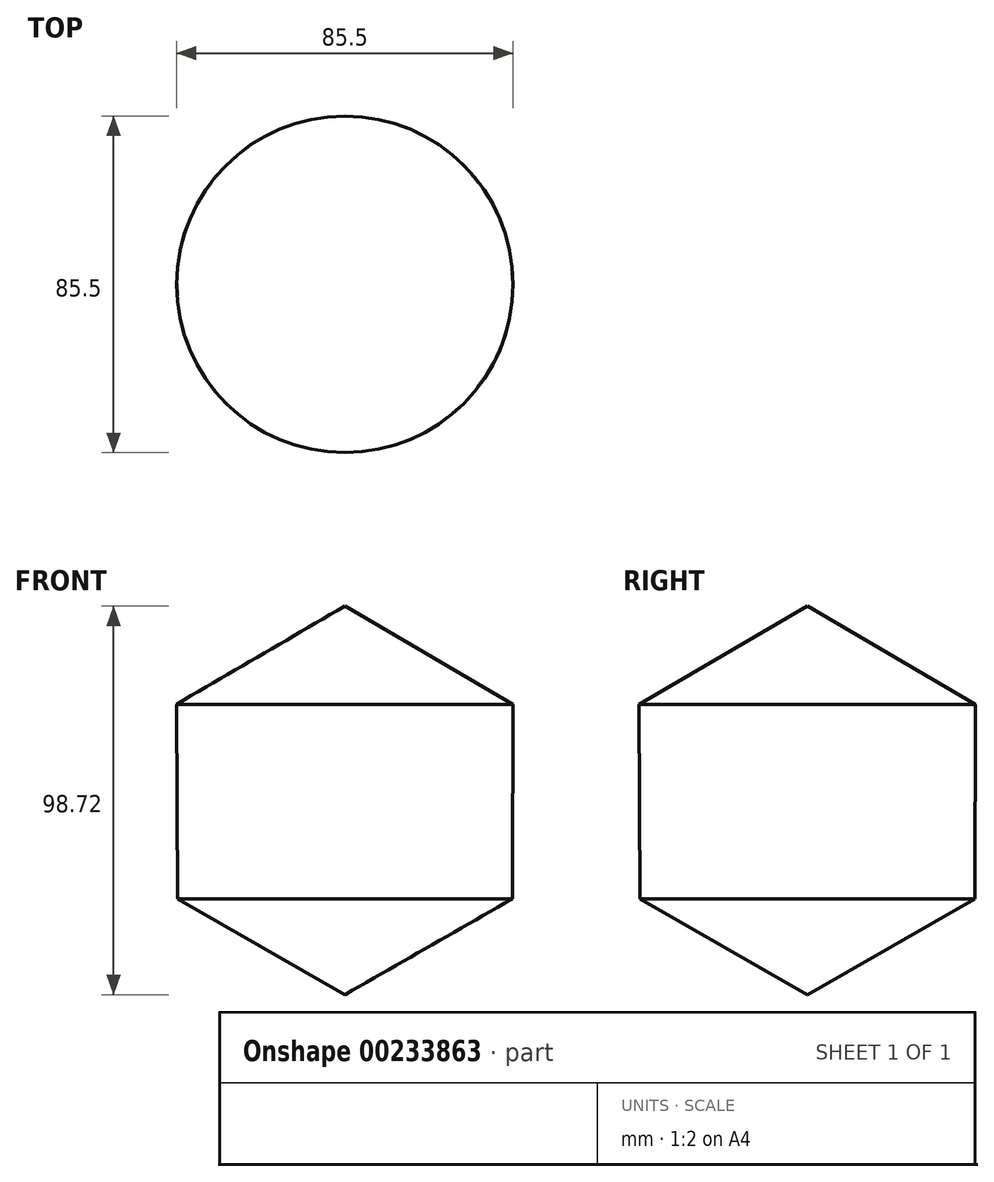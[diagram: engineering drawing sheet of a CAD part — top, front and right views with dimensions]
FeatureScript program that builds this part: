
annotation { "Feature Type Name" : "Feature", "Feature Type Description" : "" }
export const myFeature = defineFeature(function(context is Context, id is Id, definition is map)
    precondition{}
    {
        {
            var Q0;
            Q0=qCreatedBy(makeId("Front.planeOp"),FACE);
            var sketch = newSketch(context, id + "F0", { "sketchPlane" : qUnion([Q0])});
            skCircle(sketch, "E0.cCircle", {"center": v(0, 0) * mm, "radius": 42.85 * mm, "construction": true});
            skLineSegment(sketch, "E0.0", {"start": v(42.75, -24.92) * mm, "end": v(-0.2, -49.48) * mm});
            skLineSegment(sketch, "E0.1", {"start": v(-0.2, -49.48) * mm, "end": v(-42.96, -24.56) * mm});
            skLineSegment(sketch, "E0.2", {"start": v(-42.96, -24.56) * mm, "end": v(-42.75, 24.92) * mm});
            skLineSegment(sketch, "E0.3", {"start": v(-42.75, 24.92) * mm, "end": v(0.2, 49.48) * mm});
            skLineSegment(sketch, "E0.4", {"start": v(0.2, 49.48) * mm, "end": v(42.96, 24.56) * mm});
            skLineSegment(sketch, "E0.5", {"start": v(42.96, 24.56) * mm, "end": v(42.75, -24.92) * mm});
            skPoint(sketch, "E0.0.midPoint", {"position": v(21.27, -37.2) * mm});
            skLineSegment(sketch, "E1", {"start": v(0.2, 60.93) * mm, "end": v(0.2, -70.75) * mm});
            skSolve(sketch);
        }
        {
            var Q0;
            {var subQ4=sQuery(id+"F0.wireOp",EDGE,"E0.4");Q0=makeQuery(id+"F0.imprint","IMPRINT",FACE,{"disambiguationData":[TD([[makeQuery(id+"F0.imprint","IMPRINT",EDGE,{"derivedFrom":subQ4}),-1.0]])]});}
            var Q1;
            Q1=sQuery(id+"F0.wireOp",EDGE,"E1");
            revolve(context, id + "F1", {"entities" : qUnion([Q0]), "axis" : qUnion([Q1]), "revolveType" : RevolveType.FULL});
        }
    });
